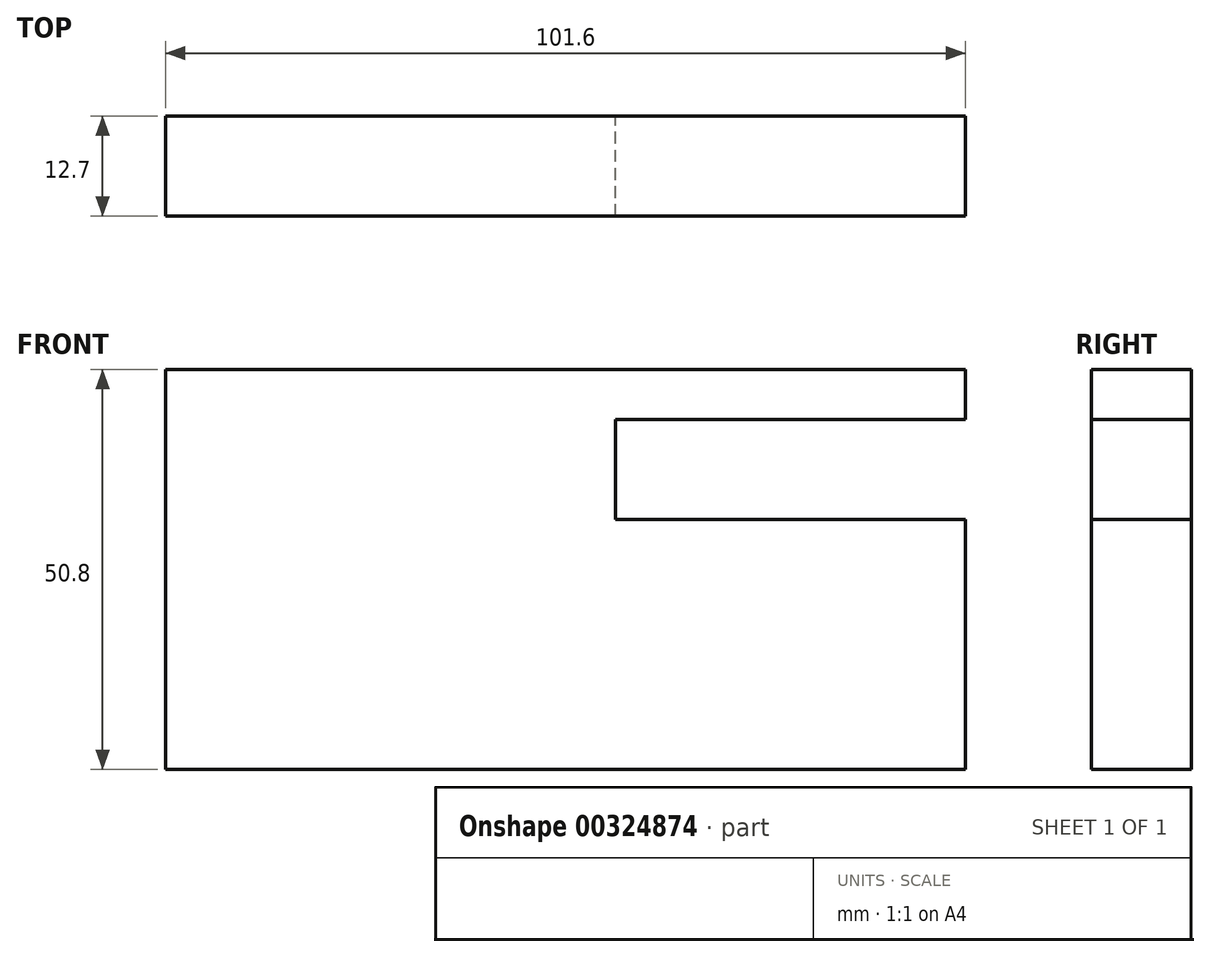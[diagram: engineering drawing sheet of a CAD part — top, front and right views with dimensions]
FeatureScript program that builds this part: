
annotation { "Feature Type Name" : "Feature", "Feature Type Description" : "" }
export const myFeature = defineFeature(function(context is Context, id is Id, definition is map)
    precondition{}
    {
        {
            var Q0;
            Q0=qCreatedBy(makeId("Front.planeOp"),FACE);
            var sketch = newSketch(context, id + "F0", { "sketchPlane" : qUnion([Q0])});
            skLineSegment(sketch, "E0", {"start": v(0, 0) * mm, "end": v(0, 50.8) * mm});
            skLineSegment(sketch, "E1", {"start": v(0, 50.8) * mm, "end": v(101.6, 50.8) * mm});
            skLineSegment(sketch, "E2", {"start": v(101.6, 0) * mm, "end": v(0, 0) * mm});
            skLineSegment(sketch, "E3.0", {"start": v(57.15, 44.45) * mm, "end": v(101.6, 44.45) * mm});
            skLineSegment(sketch, "E4.0", {"start": v(57.15, 31.75) * mm, "end": v(101.6, 31.75) * mm});
            skLineSegment(sketch, "E5", {"start": v(101.6, 50.8) * mm, "end": v(101.6, 44.45) * mm});
            skLineSegment(sketch, "E6.0", {"start": v(57.15, 44.45) * mm, "end": v(57.15, 31.75) * mm});
            skLineSegment(sketch, "E7.trimOffspring", {"start": v(101.6, 31.75) * mm, "end": v(101.6, 0) * mm});
            skSolve(sketch);
        }
        {
            var Q0;
            Q0 = qSketchRegion(id + "F0", true);
            extrude(context, id + "F1", {"entities" : qUnion([Q0]), "depth" : 12.7 * mm});
        }
    });
